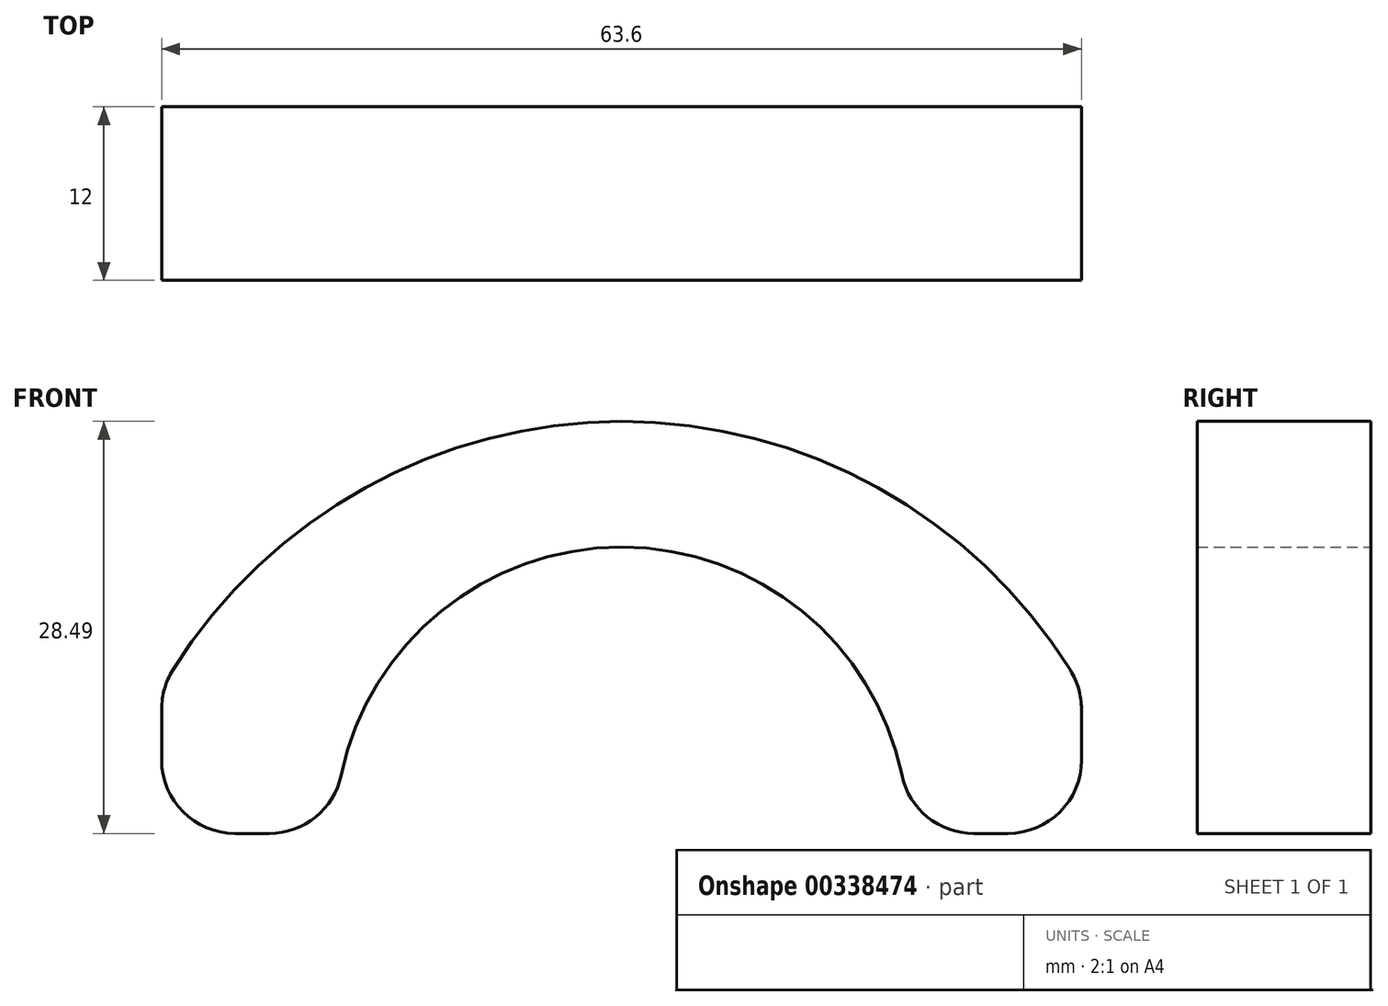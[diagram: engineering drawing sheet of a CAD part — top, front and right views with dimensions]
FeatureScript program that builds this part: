
annotation { "Feature Type Name" : "Feature", "Feature Type Description" : "" }
export const myFeature = defineFeature(function(context is Context, id is Id, definition is map)
    precondition{}
    {
        {
            var Q0;
            Q0=qCreatedBy(makeId("Front.planeOp"),FACE);
            var sketch = newSketch(context, id + "F0", { "sketchPlane" : qUnion([Q0])});
            skArc(sketch, "E0", {"start": v(19.8, 0) * mm, "mid": v(0, 19.8) * mm, "end": v(-19.8, 0) * mm});
            skLineSegment(sketch, "E1", {"start": v(-19.8, 0) * mm, "end": v(-31.8, 0) * mm});
            skLineSegment(sketch, "E2", {"start": v(-31.8, 0) * mm, "end": v(-31.8, 10) * mm});
            skLineSegment(sketch, "E3", {"start": v(19.8, 0) * mm, "end": v(31.8, 0) * mm});
            skLineSegment(sketch, "E4", {"start": v(31.8, 0) * mm, "end": v(31.8, 10) * mm});
            skArc(sketch, "E5", {"start": v(31.8, 10) * mm, "mid": v(0, 28.49) * mm, "end": v(-31.8, 10) * mm});
            skPoint(sketch, "E6.end.orphan", {"position": v(0, 14.72) * mm});
            skSolve(sketch);
        }
        {
            var Q0;
            Q0 = qSketchRegion(id + "F0", true);
            extrude(context, id + "F1", {"entities" : qUnion([Q0]), "depth" : 12 * mm});
        }
        {
            var Q0;
            Q0=makeQuery(id+"F1.opExtrude","SWEPT_EDGE",EDGE,{"disambiguationData":[OSD([sQuery(id+"F0.wireOp",EDGE,"E4"),sQuery(id+"F0.wireOp",EDGE,"E5")])]});
            var Q1;
            Q1=makeQuery(id+"F1.opExtrude","SWEPT_EDGE",EDGE,{"disambiguationData":[OSD([sQuery(id+"F0.wireOp",EDGE,"E3"),sQuery(id+"F0.wireOp",EDGE,"E4")])]});
            var Q2;
            Q2=makeQuery(id+"F1.opExtrude","SWEPT_EDGE",EDGE,{"disambiguationData":[OSD([sQuery(id+"F0.wireOp",EDGE,"E2"),sQuery(id+"F0.wireOp",EDGE,"E5")])]});
            var Q3;
            Q3=makeQuery(id+"F1.opExtrude","SWEPT_EDGE",EDGE,{"disambiguationData":[OSD([sQuery(id+"F0.wireOp",EDGE,"E1"),sQuery(id+"F0.wireOp",EDGE,"E2")])]});
            fillet(context, id + "F2", {"entities" : qUnion([Q0, Q1, Q2, Q3]), "radius" : 5.08 * mm, "tangentPropagation" : true, "allowEdgeOverflow" : false});
        }
        {
            var Q0;
            Q0=makeQuery(id+"F1.opExtrude","SWEPT_EDGE",EDGE,{"disambiguationData":[OSD([sQuery(id+"F0.wireOp",EDGE,"E0"),sQuery(id+"F0.wireOp",EDGE,"E3")])]});
            var Q1;
            Q1=makeQuery(id+"F1.opExtrude","SWEPT_EDGE",EDGE,{"disambiguationData":[OSD([sQuery(id+"F0.wireOp",EDGE,"E0"),sQuery(id+"F0.wireOp",EDGE,"E1")])]});
            fillet(context, id + "F3", {"entities" : qUnion([Q0, Q1]), "radius" : 5.08 * mm, "tangentPropagation" : true, "allowEdgeOverflow" : false});
        }
    });
